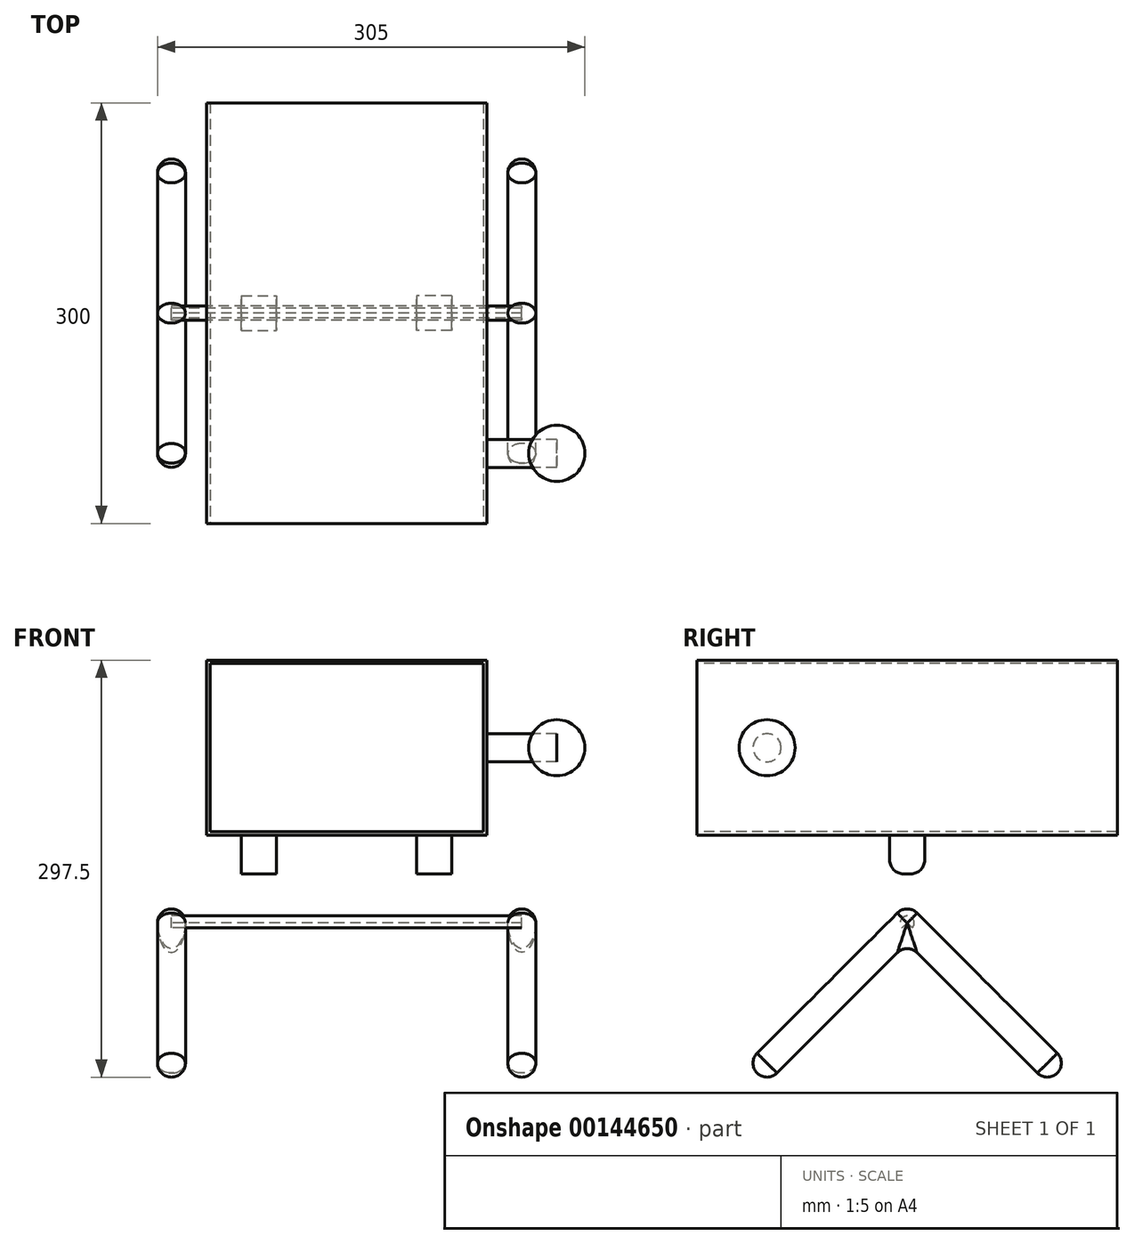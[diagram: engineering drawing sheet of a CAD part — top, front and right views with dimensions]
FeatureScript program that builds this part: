
annotation { "Feature Type Name" : "Feature", "Feature Type Description" : "" }
export const myFeature = defineFeature(function(context is Context, id is Id, definition is map)
    precondition{}
    {
        {
            var Q0;
            Q0=qCreatedBy(makeId("Front.planeOp"),FACE);
            var sketch = newSketch(context, id + "F0", { "sketchPlane" : qUnion([Q0])});
            skLineSegment(sketch, "E0", {"start": v(0, 0) * mm, "end": v(-125, 0) * mm, "construction": true});
            skSolve(sketch);
        }
        {
            var Q0;
            Q0=sQuery(id+"F0.wireOp",VERTEX,"E0.end");
            var Q1;
            Q1=sQuery(id+"F0.wireOp",EDGE,"E0");
            cPlane(context, id + "F1", {"entities" : qUnion([Q0, Q1]), "cplaneType" : CPlaneType.LINE_POINT, "offset" : 25 * mm, "width" : 150 * mm, "height" : 150 * mm});
        }
        {
            var Q0;
            Q0=qCreatedBy(id+"F1.planeOp",FACE);
            var sketch = newSketch(context, id + "F2", { "sketchPlane" : qUnion([Q0])});
            skLineSegment(sketch, "E1.bottom", {"start": v(0, 0) * mm, "end": v(-200, 0) * mm, "construction": true});
            skLineSegment(sketch, "E1.top", {"start": v(0, 100) * mm, "end": v(-200, 100) * mm, "construction": true});
            skLineSegment(sketch, "E1.left", {"start": v(0, 0) * mm, "end": v(0, 100) * mm, "construction": true});
            skLineSegment(sketch, "E1.right", {"start": v(-200, 0) * mm, "end": v(-200, 100) * mm, "construction": true});
            skLineSegment(sketch, "E2", {"start": v(0, 0) * mm, "end": v(-100, 100) * mm});
            skLineSegment(sketch, "E3", {"start": v(-100, 100) * mm, "end": v(-200, 0) * mm});
            skLineSegment(sketch, "E4", {"start": v(-100, 100) * mm, "end": v(-100, 0) * mm, "construction": true});
            skCircle(sketch, "E5", {"center": v(-100, 100) * mm, "radius": 5 * mm});
            skSolve(sketch);
        }
        {
            var Q0;
            Q0=sQuery(id+"F2.wireOp",VERTEX,"E2.start");
            var Q1;
            Q1=sQuery(id+"F2.wireOp",EDGE,"E2");
            cPlane(context, id + "F3", {"entities" : qUnion([Q0, Q1]), "cplaneType" : CPlaneType.LINE_POINT, "offset" : 25 * mm, "width" : 150 * mm, "height" : 150 * mm});
        }
        {
            var Q0;
            Q0=qCreatedBy(id+"F3.planeOp",FACE);
            var sketch = newSketch(context, id + "F4", { "sketchPlane" : qUnion([Q0])});
            skCircle(sketch, "E6", {"center": v(125, 0) * mm, "radius": 10 * mm});
            skLineSegment(sketch, "E7", {"start": v(135, 0) * mm, "end": v(115, 0) * mm});
            skSolve(sketch);
        }
        {
            var Q0;
            Q0=makeQuery(id+"F4.imprint","IMPRINT",FACE,{"disambiguationData":[TD([[makeQuery(id+"F4.imprint","IMPRINT",EDGE,{"derivedFrom":sQuery(id+"F4.wireOp",EDGE,"E6")}),1.0]])]});
            var Q1;
            Q1=sQuery(id+"F2.wireOp",EDGE,"E2");
            var Q2;
            Q2=sQuery(id+"F2.wireOp",EDGE,"E3");
            sweep(context, id + "F5", {"profiles" : qUnion([Q0]), "path" : qUnion([Q1, Q2])});
        }
        {
            var Q0;
            {var subQ0=sQuery(id+"F4.wireOp",EDGE,"E7");Q0=makeQuery(id+"F4.imprint","IMPRINT",FACE,{"disambiguationData":[TD([[makeQuery(id+"F4.imprint","IMPRINT",EDGE,{"derivedFrom":subQ0}),-1.0]])]});}
            var Q1;
            Q1=sQuery(id+"F0.wireOp",EDGE,"E0");
            revolve(context, id + "F6", {"entities" : qUnion([Q0]), "axis" : qUnion([Q1]), "revolveType" : RevolveType.ONE_DIRECTION, "oppositeDirection" : true, "angle" : 180 * degree});
        }
        {
            var Q0;
            Q0=sQuery(id+"F2.wireOp",EDGE,"E4");
            var Q1;
            Q1=sQuery(id+"F2.wireOp",EDGE,"E1.left");
            cPlane(context, id + "F7", {"entities" : qUnion([Q0, Q1]), "cplaneType" : CPlaneType.LINE_ANGLE, "offset" : 25 * mm, "angle" : 90 * degree, "width" : 150 * mm, "height" : 150 * mm});
        }
        {
            var Q0;
            Q0=makeQuery(id+"F6.opRevolve","SWEPT_BODY",BODY,{"disambiguationData":[OSD([sQuery(id+"F4.wireOp",EDGE,"E6"),sQuery(id+"F4.wireOp",EDGE,"E7")])]});
            var Q1;
            Q1=qCreatedBy(id+"F7.planeOp",FACE);
            mirror(context, id + "F8", {"entities" : qUnion([Q0]), "mirrorPlane" : qUnion([Q1])});
        }
        {
            var Q0;
            Q0=makeQuery(id+"F5.opSweep","MID_CAP_EDGE",EDGE,{"disambiguationData":[OSD([sQuery(id+"F2.wireOp",VERTEX,"E3.start"),sQuery(id+"F4.wireOp",EDGE,"E6")])],"capPos":1.0});
            fillet(context, id + "F9", {"entities" : qUnion([Q0]), "radius" : 10 * mm, "tangentPropagation" : true, "allowEdgeOverflow" : false});
        }
        {
            var Q0;
            Q0=makeQuery(id+"F5.opSweep","SWEPT_BODY",BODY,{"disambiguationData":[OSD([sQuery(id+"F2.wireOp",EDGE,"E3"),sQuery(id+"F4.wireOp",EDGE,"E6")])]});
            var Q1;
            Q1=makeQuery(id+"F6.opRevolve","SWEPT_BODY",BODY,{"disambiguationData":[OSD([sQuery(id+"F4.wireOp",EDGE,"E6"),sQuery(id+"F4.wireOp",EDGE,"E7")])]});
            var Q2;
            Q2=makeQuery(id+"F8.opPattern","COPY",BODY,{"derivedFrom":makeQuery(id+"F6.opRevolve","SWEPT_BODY",BODY,{"disambiguationData":[OSD([sQuery(id+"F4.wireOp",EDGE,"E6"),sQuery(id+"F4.wireOp",EDGE,"E7")])]}),"instanceName":"1"});
            var Q3;
            Q3=qCreatedBy(makeId("Right.planeOp"),FACE);
            mirror(context, id + "F10", {"entities" : qUnion([Q0, Q1, Q2]), "mirrorPlane" : qUnion([Q3])});
        }
        {
            var Q0;
            {var subQ0=sQuery(id+"F2.wireOp",EDGE,"E3");var subQ1=sQuery(id+"F2.wireOp",EDGE,"E2");var subQ2=makeQuery(id+"F2.imprint","INTERSECT",VERTEX,{"derivedFrom":[subQ1,subQ0]});Q0=makeQuery(id+"F2.imprint","IMPRINT",FACE,{"disambiguationData":[TD([[makeQuery(id+"F2.imprint","IMPRINT",EDGE,{"disambiguationData":[TD([[subQ2,1.0]])],"derivedFrom":subQ1}),-1.0]])]});}
            extrude(context, id + "F11", {"entities" : qUnion([Q0]), "oppositeDirection" : true, "depth" : 250 * mm});
        }
        {
            var Q0;
            Q0=qCreatedBy(makeId("Front.planeOp"),FACE);
            var sketch = newSketch(context, id + "F12", { "sketchPlane" : qUnion([Q0])});
            skLineSegment(sketch, "E8", {"start": v(0, 0) * mm, "end": v(0, 300) * mm, "construction": true});
            skLineSegment(sketch, "E9.bottom", {"start": v(-100, 287.5) * mm, "end": v(100, 287.5) * mm});
            skLineSegment(sketch, "E9.top", {"start": v(-100, 162.5) * mm, "end": v(100, 162.5) * mm});
            skLineSegment(sketch, "E9.left", {"start": v(-100, 287.5) * mm, "end": v(-100, 162.5) * mm});
            skLineSegment(sketch, "E9.right", {"start": v(100, 287.5) * mm, "end": v(100, 162.5) * mm});
            skPoint(sketch, "E9.middle", {"position": v(0, 225) * mm});
            skSolve(sketch);
        }
        {
            var Q0;
            Q0=makeQuery(id+"F12.imprint","IMPRINT",FACE,{"disambiguationData":[TD([[makeQuery(id+"F12.imprint","IMPRINT",EDGE,{"derivedFrom":sQuery(id+"F12.wireOp",EDGE,"E9.bottom")}),-1.0]])]});
            extrude(context, id + "F13", {"entities" : qUnion([Q0]), "oppositeDirection" : true, "depth" : 250 * mm});
        }
        {
            var Q0;
            Q0=makeQuery(id+"F13.opExtrude","CAP_FACE",FACE,{"disambiguationData":[OSD([sQuery(id+"F12.wireOp",EDGE,"E9.bottom"),sQuery(id+"F12.wireOp",EDGE,"E9.top"),sQuery(id+"F12.wireOp",EDGE,"E9.left"),sQuery(id+"F12.wireOp",EDGE,"E9.right")])],"isStart":true});
            extrude(context, id + "F14", {"entities" : qUnion([Q0]), "operationType" : NewBodyOperationType.ADD, "depth" : 50 * mm});
        }
        {
            var Q0;
            Q0=qCreatedBy(makeId("Right.planeOp"),FACE);
            cPlane(context, id + "F15", {"entities" : qUnion([Q0]), "cplaneType" : CPlaneType.OFFSET, "offset" : 75 * mm, "width" : 150 * mm, "height" : 150 * mm});
        }
        {
            var Q0;
            Q0=qCreatedBy(id+"F15.planeOp",FACE);
            var sketch = newSketch(context, id + "F16", { "sketchPlane" : qUnion([Q0])});
            skLineSegment(sketch, "E10", {"start": v(0, 0) * mm, "end": v(100, 0) * mm, "construction": true});
            skLineSegment(sketch, "E11", {"start": v(100, 0) * mm, "end": v(100, 150) * mm, "construction": true});
            skLineSegment(sketch, "E12.bottom", {"start": v(87.5, 165) * mm, "end": v(112.5, 165) * mm});
            skLineSegment(sketch, "E12.top", {"start": v(97.5, 135) * mm, "end": v(102.5, 135) * mm});
            skLineSegment(sketch, "E12.left", {"start": v(87.5, 165) * mm, "end": v(87.5, 145) * mm});
            skLineSegment(sketch, "E12.right", {"start": v(112.5, 165) * mm, "end": v(112.5, 145) * mm});
            skPoint(sketch, "E12.middle", {"position": v(100, 150) * mm});
            skPoint(sketch, "E13.visualSharp", {"position": v(87.5, 135) * mm});
            skArc(sketch, "E13.filletArc", {"start": v(87.5, 145) * mm, "mid": v(90.43, 137.93) * mm, "end": v(97.5, 135) * mm});
            skPoint(sketch, "E14.visualSharp", {"position": v(112.5, 135) * mm});
            skArc(sketch, "E14.filletArc", {"start": v(102.5, 135) * mm, "mid": v(109.57, 137.93) * mm, "end": v(112.5, 145) * mm});
            skSolve(sketch);
        }
        {
            var Q0;
            Q0=makeQuery(id+"F16.imprint","IMPRINT",FACE,{"disambiguationData":[TD([[makeQuery(id+"F16.imprint","IMPRINT",EDGE,{"derivedFrom":sQuery(id+"F16.wireOp",EDGE,"E12.bottom")}),-1.0]])]});
            extrude(context, id + "F17", {"entities" : qUnion([Q0]), "operationType" : NewBodyOperationType.ADD, "oppositeDirection" : true, "depth" : 25 * mm});
        }
        {
            var Q0;
            Q0=makeQuery(id+"F13.opExtrude","SWEPT_BODY",BODY,{"disambiguationData":[OSD([sQuery(id+"F12.wireOp",EDGE,"E9.bottom"),sQuery(id+"F12.wireOp",EDGE,"E9.top"),sQuery(id+"F12.wireOp",EDGE,"E9.left"),sQuery(id+"F12.wireOp",EDGE,"E9.right")])]});
            var Q1;
            Q1=qCreatedBy(makeId("Right.planeOp"),FACE);
            mirror(context, id + "F18", {"entities" : qUnion([Q0]), "mirrorPlane" : qUnion([Q1])});
        }
        {
            var Q0;
            Q0=makeQuery(id+"F18.opPattern","COPY",FACE,{"derivedFrom":makeQuery(id+"F14.opExtrude","CAP_FACE",FACE,{"disambiguationData":[OSD([sQuery(id+"F12.wireOp",EDGE,"E9.bottom"),sQuery(id+"F12.wireOp",EDGE,"E9.top"),sQuery(id+"F12.wireOp",EDGE,"E9.left"),sQuery(id+"F12.wireOp",EDGE,"E9.right")])],"isStart":false}),"instanceName":"1"});
            var sketch = newSketch(context, id + "F19", { "sketchPlane" : qUnion([Q0])});
            skLineSegment(sketch, "E15.bottom", {"start": v(97.5, 285) * mm, "end": v(-97.5, 285) * mm});
            skLineSegment(sketch, "E15.top", {"start": v(97.5, 165) * mm, "end": v(-97.5, 165) * mm});
            skLineSegment(sketch, "E15.left", {"start": v(97.5, 285) * mm, "end": v(97.5, 165) * mm});
            skLineSegment(sketch, "E15.right", {"start": v(-97.5, 285) * mm, "end": v(-97.5, 165) * mm});
            skPoint(sketch, "E15.middle", {"position": v(0, 225) * mm});
            skPoint(sketch, "E15.middle.positionSnap0", {"position": v(-100, 225) * mm});
            skPoint(sketch, "E15.middle.positionSnap1", {"position": v(0, 162.5) * mm});
            skPoint(sketch, "E15.centerSnap0", {"position": v(-100, 225) * mm});
            skPoint(sketch, "E15.centerSnap1", {"position": v(0, 162.5) * mm});
            skSolve(sketch);
        }
        {
            var Q0;
            Q0 = qSketchRegion(id + "F19", true);
            extrude(context, id + "F20", {"entities" : qUnion([Q0]), "operationType" : NewBodyOperationType.REMOVE, "endBound" : BoundingType.THROUGH_ALL, "oppositeDirection" : true, "depth" : 25 * mm});
        }
        {
            var Q0;
            {var subQ0=sQuery(id+"F12.wireOp",EDGE,"E9.right");Q0=makeQuery(id+"F14.boolean.opBoolean","MERGE",FACE,{"derivedFrom":[makeQuery(id+"F13.opExtrude","SWEPT_FACE",FACE,{"disambiguationData":[OSD([subQ0])]}),makeQuery(id+"F14.opExtrude","SWEPT_FACE",FACE,{"disambiguationData":[OSD([subQ0])]})]});}
            var sketch = newSketch(context, id + "F21", { "sketchPlane" : qUnion([Q0])});
            skCircle(sketch, "E16", {"center": v(0, 225) * mm, "radius": 10 * mm});
            skPoint(sketch, "E16.centerSnap0", {"position": v(-50, 225) * mm});
            skSolve(sketch);
        }
        {
            var Q0;
            Q0 = qSketchRegion(id + "F21", true);
            extrude(context, id + "F22", {"entities" : qUnion([Q0]), "depth" : 50 * mm});
        }
        {
            var Q0;
            Q0=makeQuery(id+"F22.opExtrude","CAP_FACE",FACE,{"disambiguationData":[OSD([sQuery(id+"F21.wireOp",EDGE,"E16")])],"isStart":false});
            var sketch = newSketch(context, id + "F23", { "sketchPlane" : qUnion([Q0])});
            skCircle(sketch, "E17", {"center": v(0, 225) * mm, "radius": 20 * mm});
            skLineSegment(sketch, "E18", {"start": v(0, 205) * mm, "end": v(0, 245) * mm});
            skSolve(sketch);
        }
        {
            var Q0;
            {var subQ0=sQuery(id+"F23.wireOp",EDGE,"E18");var subQ1=sQuery(id+"F23.wireOp",EDGE,"E17");var subQ2=makeQuery(id+"F23.imprint","INTERSECT",VERTEX,{"disambiguationData":[OD(0.0)],"derivedFrom":[subQ1,subQ0]});Q0=makeQuery(id+"F23.imprint","IMPRINT",FACE,{"disambiguationData":[TD([[makeQuery(id+"F23.imprint","IMPRINT",EDGE,{"disambiguationData":[TD([[subQ2,1.0]])],"derivedFrom":subQ1}),1.0]])]});}
            var Q1;
            {var subQ0=sQuery(id+"F23.wireOp",EDGE,"E18");var subQ1=makeQuery(id+"F22.opExtrude","CAP_EDGE",EDGE,{"disambiguationData":[OSD([sQuery(id+"F21.wireOp",EDGE,"E16")])],"isStart":false});var subQ2=makeQuery(id+"F23.imprint","INTERSECT",VERTEX,{"disambiguationData":[OD(0.0)],"derivedFrom":[subQ1,subQ0]});Q1=makeQuery(id+"F23.imprint","IMPRINT",FACE,{"disambiguationData":[TD([[makeQuery(id+"F23.imprint","IMPRINT",EDGE,{"disambiguationData":[TD([[subQ2,-1.0]])],"derivedFrom":subQ0}),1.0]])]});}
            var Q2;
            Q2=sQuery(id+"F23.wireOp",EDGE,"E18");
            revolve(context, id + "F24", {"entities" : qUnion([Q0, Q1]), "axis" : qUnion([Q2]), "revolveType" : RevolveType.FULL});
        }
    });
